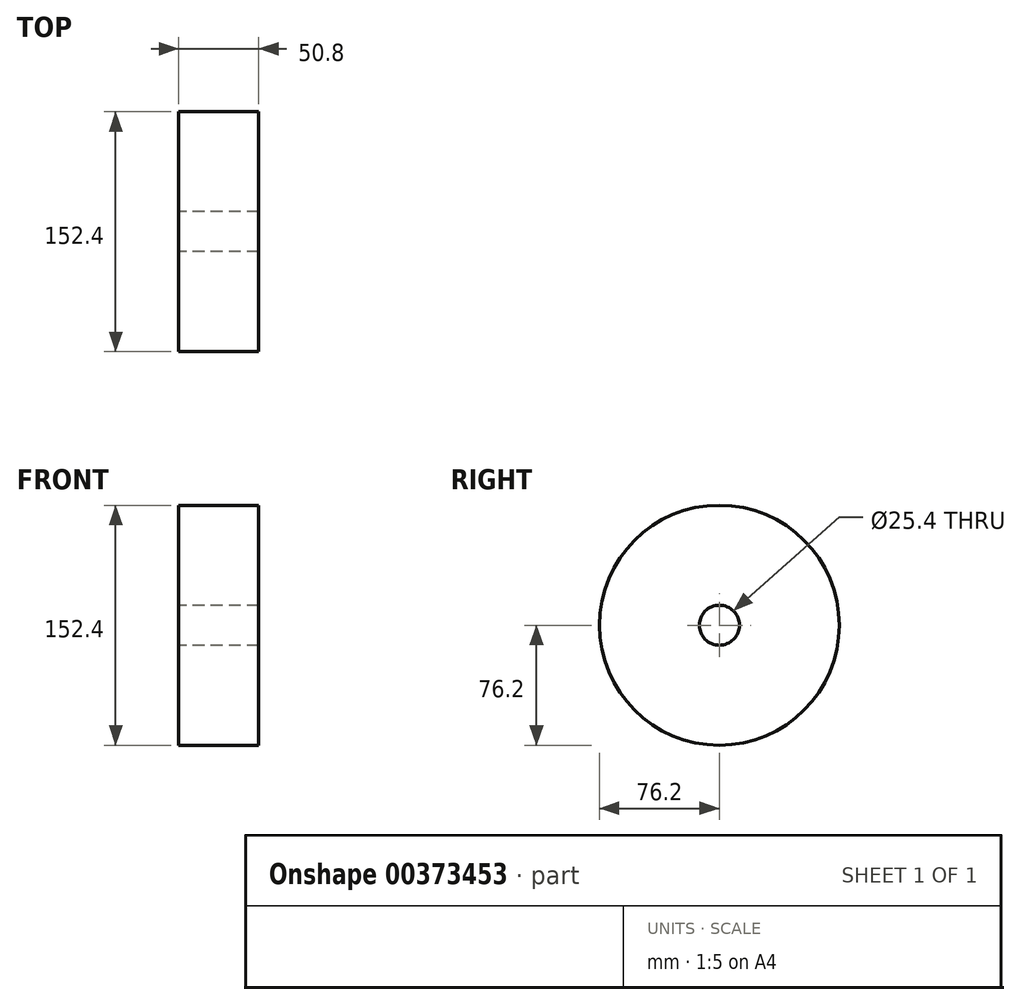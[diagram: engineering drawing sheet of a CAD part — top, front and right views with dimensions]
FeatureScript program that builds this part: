
annotation { "Feature Type Name" : "Feature", "Feature Type Description" : "" }
export const myFeature = defineFeature(function(context is Context, id is Id, definition is map)
    precondition{}
    {
        {
            var Q0;
            Q0=qCreatedBy(makeId("Right.planeOp"),FACE);
            var sketch = newSketch(context, id + "F0", { "sketchPlane" : qUnion([Q0])});
            skCircle(sketch, "E0", {"center": v(0, 0) * mm, "radius": 76.2 * mm});
            skCircle(sketch, "E1", {"center": v(0, 0) * mm, "radius": 12.7 * mm});
            skSolve(sketch);
        }
        {
            var Q0;
            Q0 = qSketchRegion(id + "F0", true);
            extrude(context, id + "F1", {"entities" : qUnion([Q0]), "endBound" : BoundingType.SYMMETRIC, "depth" : 50.8 * mm});
        }
    });
